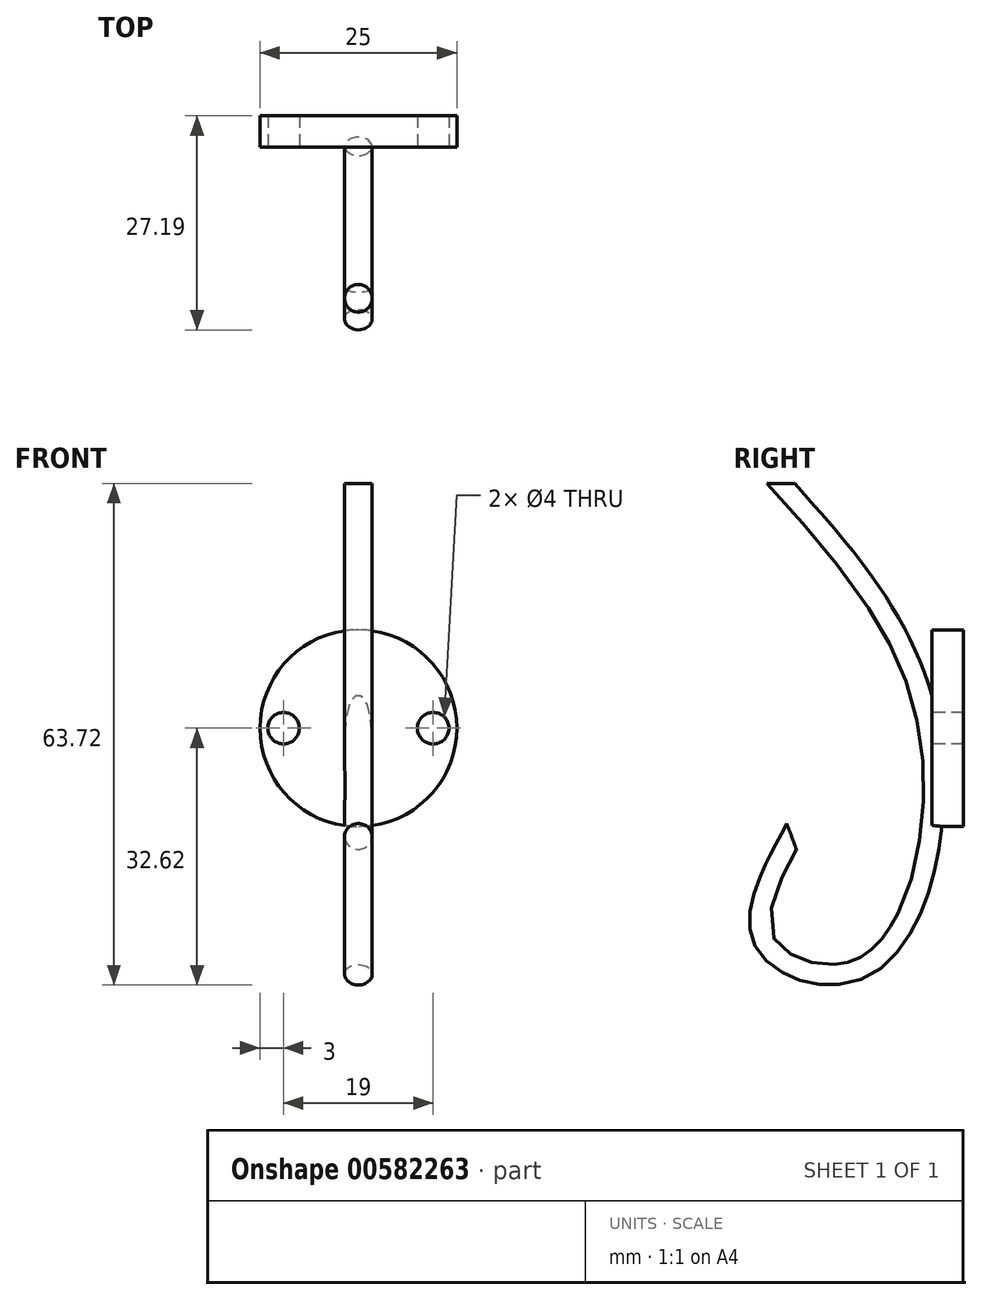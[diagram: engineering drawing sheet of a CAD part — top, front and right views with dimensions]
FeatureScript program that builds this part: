
annotation { "Feature Type Name" : "Feature", "Feature Type Description" : "" }
export const myFeature = defineFeature(function(context is Context, id is Id, definition is map)
    precondition{}
    {
        {
            var Q0;
            Q0=qCreatedBy(makeId("Front.planeOp"),FACE);
            var sketch = newSketch(context, id + "F0", { "sketchPlane" : qUnion([Q0])});
            skCircle(sketch, "E0", {"center": v(0, 0) * mm, "radius": 12.5 * mm});
            skSolve(sketch);
        }
        {
            var Q0;
            Q0 = qSketchRegion(id + "F0", true);
            extrude(context, id + "F1", {"entities" : qUnion([Q0]), "depth" : 4 * mm, "offsetDistance" : 25 * mm});
        }
        {
            var Q0;
            Q0=makeQuery(id+"F1.opExtrude","CAP_FACE",FACE,{"disambiguationData":[OSD([sQuery(id+"F0.wireOp",EDGE,"E0")])],"isStart":false});
            var sketch = newSketch(context, id + "F2", { "sketchPlane" : qUnion([Q0])});
            skCircle(sketch, "E1", {"center": v(-9.5, 0) * mm, "radius": 2 * mm});
            skCircle(sketch, "E2.MirrorC", {"center": v(9.5, 0) * mm, "radius": 2 * mm});
            skSolve(sketch);
        }
        {
            var Q0;
            Q0 = qSketchRegion(id + "F2", true);
            extrude(context, id + "F3", {"entities" : qUnion([Q0]), "operationType" : NewBodyOperationType.REMOVE, "oppositeDirection" : true, "depth" : 25 * mm, "offsetDistance" : 25 * mm});
        }
        {
            var Q0;
            Q0=qCreatedBy(makeId("Right.planeOp"),FACE);
            var sketch = newSketch(context, id + "F4", { "sketchPlane" : qUnion([Q0])});
            skPoint(sketch, "E3.3.internal.snap0", {"position": v(-25.05, 31.05) * mm});
            skFitSpline(sketch, "E3", {"points": [v(-23.22, 31.05) * mm, v(-4.46, 0) * mm, v(-12.5, -30.1) * mm, v(-25.05, -27.18) * mm, v(-21.76, -13.78) * mm], "startDerivative": vector(77.78, -86.82) * mm, "endDerivative": vector(39.98, 75.66) * mm});
            skSolve(sketch);
        }
        {
            var Q0;
            Q0=qCreatedBy(makeId("Top.planeOp"),FACE);
            cPlane(context, id + "F5", {"entities" : qUnion([Q0]), "cplaneType" : CPlaneType.OFFSET, "offset" : 31.1 * mm, "width" : 150 * mm, "height" : 150 * mm});
        }
        {
            var Q0;
            Q0=qCreatedBy(id+"F5.planeOp",FACE);
            var sketch = newSketch(context, id + "F6", { "sketchPlane" : qUnion([Q0])});
            skCircle(sketch, "E4", {"center": v(0, -23.17) * mm, "radius": 1.75 * mm});
            skSolve(sketch);
        }
        {
            var Q0;
            Q0=makeQuery(id+"F6.imprint","IMPRINT",FACE,{"disambiguationData":[TD([[makeQuery(id+"F6.imprint","IMPRINT",EDGE,{"derivedFrom":sQuery(id+"F6.wireOp",EDGE,"E4")}),1.0]])]});
            var Q1;
            Q1=sQuery(id+"F4.wireOp",EDGE,"E3");
            sweep(context, id + "F7", {"operationType" : NewBodyOperationType.ADD, "profiles" : qUnion([Q0]), "path" : qUnion([Q1])});
        }
    });
